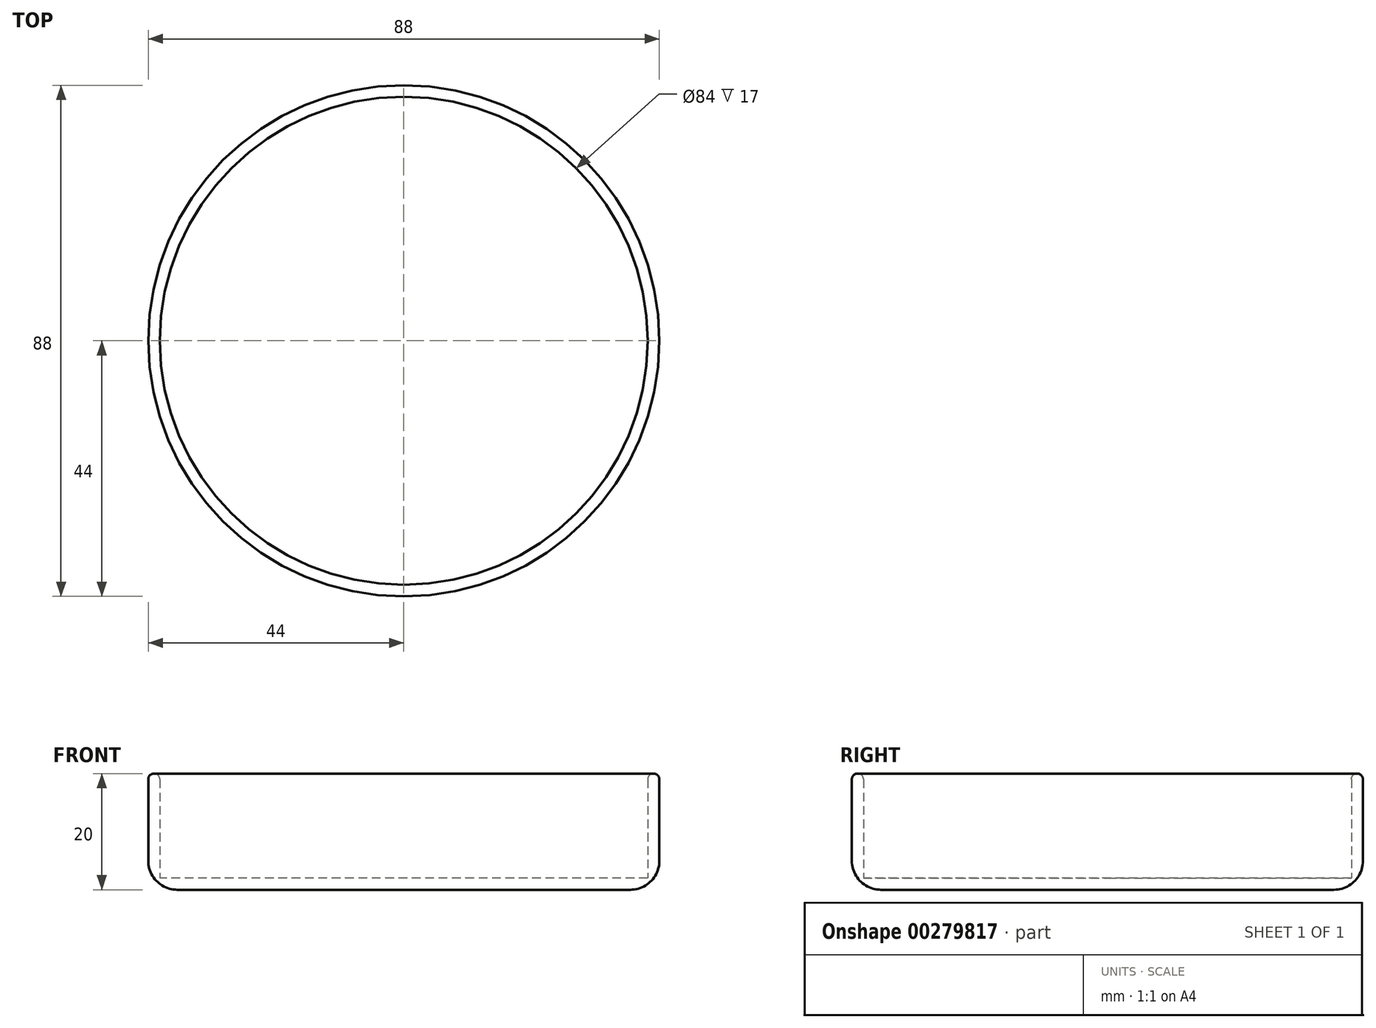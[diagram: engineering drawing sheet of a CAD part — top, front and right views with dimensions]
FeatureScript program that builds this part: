
annotation { "Feature Type Name" : "Feature", "Feature Type Description" : "" }
export const myFeature = defineFeature(function(context is Context, id is Id, definition is map)
    precondition{}
    {
        {
            var Q0;
            Q0=qCreatedBy(makeId("Top.planeOp"),FACE);
            var sketch = newSketch(context, id + "F0", { "sketchPlane" : qUnion([Q0])});
            skCircle(sketch, "E0", {"center": v(0, 0) * mm, "radius": 44 * mm});
            skSolve(sketch);
        }
        {
            var Q0;
            Q0 = qSketchRegion(id + "F0", true);
            extrude(context, id + "F1", {"entities" : qUnion([Q0]), "depth" : 20 * mm});
        }
        {
            var Q0;
            Q0=makeQuery(id+"F1.opExtrude","CAP_FACE",FACE,{"disambiguationData":[OSD([sQuery(id+"F0.wireOp",EDGE,"E0")])],"isStart":false});
            shell(context, id + "F2", {"entities" : qUnion([Q0]), "thickness" : 2 * mm});
        }
        {
            var Q0;
            {var subQ0=sQuery(id+"F0.wireOp",EDGE,"E0");Q0=makeQuery(id+"F2.opShell","OFFSET_EDGE",EDGE,{"disambiguationData":[OSD([subQ0]),TDD([makeQuery(id+"F1.opExtrude","CAP_EDGE",EDGE,{"disambiguationData":[OSD([subQ0])],"isStart":false})])]});}
            fillet(context, id + "F3", {"entities" : qUnion([Q0]), "radius" : 1 * mm, "tangentPropagation" : true, "allowEdgeOverflow" : false});
        }
        {
            var Q0;
            Q0=makeQuery(id+"F1.opExtrude","CAP_EDGE",EDGE,{"disambiguationData":[OSD([sQuery(id+"F0.wireOp",EDGE,"E0")])],"isStart":false});
            fillet(context, id + "F4", {"entities" : qUnion([Q0]), "radius" : 1 * mm, "tangentPropagation" : true, "allowEdgeOverflow" : false});
        }
        {
            var Q0;
            Q0=makeQuery(id+"F1.opExtrude","CAP_EDGE",EDGE,{"disambiguationData":[OSD([sQuery(id+"F0.wireOp",EDGE,"E0")])],"isStart":true});
            fillet(context, id + "F5", {"entities" : qUnion([Q0]), "radius" : 5 * mm, "tangentPropagation" : true, "allowEdgeOverflow" : false});
        }
    });
